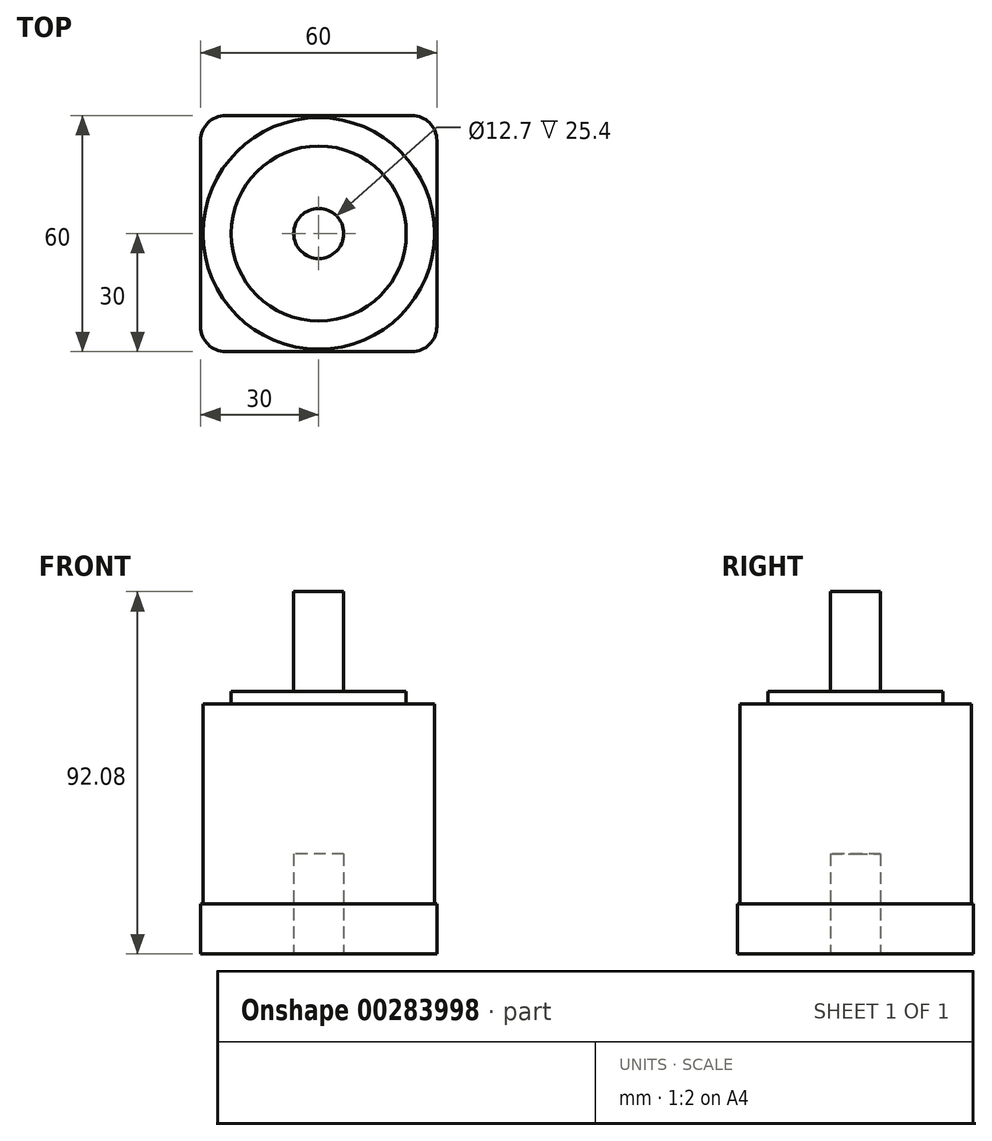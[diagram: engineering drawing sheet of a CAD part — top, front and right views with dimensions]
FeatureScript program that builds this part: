
annotation { "Feature Type Name" : "Feature", "Feature Type Description" : "" }
export const myFeature = defineFeature(function(context is Context, id is Id, definition is map)
    precondition{}
    {
        {
            var Q0;
            Q0=qCreatedBy(makeId("Top.planeOp"),FACE);
            var sketch = newSketch(context, id + "F0", { "sketchPlane" : qUnion([Q0])});
            skLineSegment(sketch, "E0.bottom", {"start": v(23.65, -30) * mm, "end": v(-23.65, -30) * mm});
            skLineSegment(sketch, "E0.top", {"start": v(23.65, 30) * mm, "end": v(-23.65, 30) * mm});
            skLineSegment(sketch, "E0.left", {"start": v(30, -23.65) * mm, "end": v(30, 23.65) * mm});
            skLineSegment(sketch, "E0.right", {"start": v(-30, -23.65) * mm, "end": v(-30, 23.65) * mm});
            skPoint(sketch, "E0.middle", {"position": v(0, 0) * mm});
            skPoint(sketch, "E1.visualSharp", {"position": v(-30, 30) * mm});
            skArc(sketch, "E1.filletArc", {"start": v(-23.65, 30) * mm, "mid": v(-28.14, 28.14) * mm, "end": v(-30, 23.65) * mm});
            skPoint(sketch, "E2.visualSharp", {"position": v(30, 30) * mm});
            skArc(sketch, "E2.filletArc", {"start": v(30, 23.65) * mm, "mid": v(28.14, 28.14) * mm, "end": v(23.65, 30) * mm});
            skPoint(sketch, "E3.visualSharp", {"position": v(-30, -30) * mm});
            skArc(sketch, "E3.filletArc", {"start": v(-30, -23.65) * mm, "mid": v(-28.14, -28.14) * mm, "end": v(-23.65, -30) * mm});
            skPoint(sketch, "E4.visualSharp", {"position": v(30, -30) * mm});
            skArc(sketch, "E4.filletArc", {"start": v(23.65, -30) * mm, "mid": v(28.14, -28.14) * mm, "end": v(30, -23.65) * mm});
            skCircle(sketch, "E5", {"center": v(0, 0) * mm, "radius": 29.41 * mm});
            skCircle(sketch, "E6", {"center": v(0, 0) * mm, "radius": 22.23 * mm});
            skCircle(sketch, "E7", {"center": v(0, 0) * mm, "radius": 6.35 * mm});
            skSolve(sketch);
        }
        {
            var Q0;
            Q0=makeQuery(id+"F0.imprint","IMPRINT",FACE,{"disambiguationData":[TD([[makeQuery(id+"F0.imprint","IMPRINT",EDGE,{"derivedFrom":sQuery(id+"F0.wireOp",EDGE,"E0.bottom")}),-1.0]])]});
            extrude(context, id + "F1", {"entities" : qUnion([Q0]), "depth" : 12.7 * mm});
        }
        {
            var Q0;
            Q0=makeQuery(id+"F0.imprint","IMPRINT",FACE,{"disambiguationData":[TD([[makeQuery(id+"F0.imprint","IMPRINT",EDGE,{"derivedFrom":sQuery(id+"F0.wireOp",EDGE,"E5")}),1.0]])]});
            extrude(context, id + "F2", {"entities" : qUnion([Q0]), "operationType" : NewBodyOperationType.ADD, "depth" : 63.5 * mm});
        }
        {
            var Q0;
            Q0=makeQuery(id+"F0.imprint","IMPRINT",FACE,{"disambiguationData":[TD([[makeQuery(id+"F0.imprint","IMPRINT",EDGE,{"derivedFrom":sQuery(id+"F0.wireOp",EDGE,"E6")}),1.0]])]});
            extrude(context, id + "F3", {"entities" : qUnion([Q0]), "operationType" : NewBodyOperationType.ADD, "depth" : 66.67 * mm});
        }
        {
            var Q0;
            Q0=makeQuery(id+"F0.imprint","IMPRINT",FACE,{"disambiguationData":[TD([[makeQuery(id+"F0.imprint","IMPRINT",EDGE,{"derivedFrom":sQuery(id+"F0.wireOp",EDGE,"E7")}),1.0]])]});
            extrude(context, id + "F4", {"entities" : qUnion([Q0]), "operationType" : NewBodyOperationType.ADD, "depth" : 92.07 * mm});
        }
        {
            var Q0;
            Q0=makeQuery(id+"F0.imprint","IMPRINT",FACE,{"disambiguationData":[TD([[makeQuery(id+"F0.imprint","IMPRINT",EDGE,{"derivedFrom":sQuery(id+"F0.wireOp",EDGE,"E7")}),1.0]])]});
            extrude(context, id + "F5", {"entities" : qUnion([Q0]), "operationType" : NewBodyOperationType.REMOVE, "depth" : 25.4 * mm});
        }
    });
